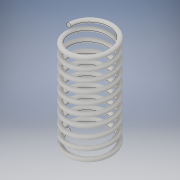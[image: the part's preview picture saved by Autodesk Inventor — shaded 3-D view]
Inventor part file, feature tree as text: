
AUTODESK INVENTOR PART (.ipt)
format: ipt  version: 2018 (Build 220112000, 112)  size: 397,824 bytes
history: native  units: in
note: dims shown in document units (in); Inventor stores cm internally (conversion verified against a paired STEP export)
features: helix x1, sketch x1
ambient origin geometry x8: Origin, YZ Plane, XZ Plane, XY Plane, X Axis, Y Axis, Z Axis, Center Point
bodies: Solid1 (feature_tree)
feature tree (2):
  helix  "Coil1"  [1 undecoded]
  sketch  "Sketch1"  dims[d1=0.1969in d2=1.0in d3=0.7657in d4=3.5433in d5=0.0in d6=90.0deg d7=90.0deg d8=90.0deg d9=90.0deg]
note: 1 required parameter value undecoded (feature->parameter linkage not recoverable at this tier; creation-order binding heuristic only, values carry confidence <= 0.55)
